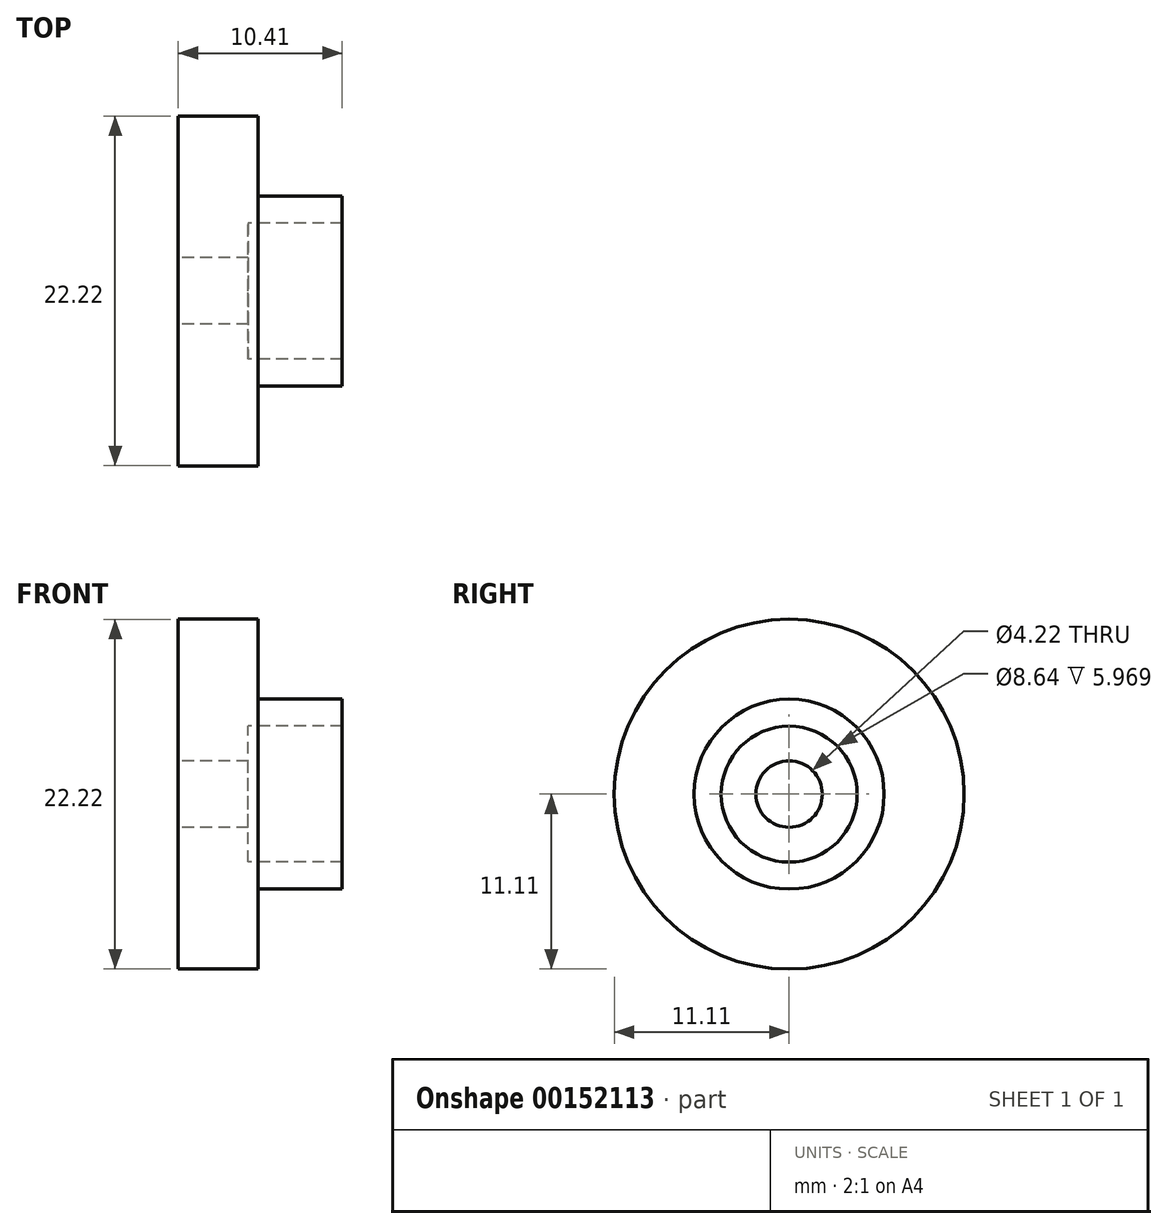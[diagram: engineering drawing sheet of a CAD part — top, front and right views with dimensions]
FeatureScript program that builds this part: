
annotation { "Feature Type Name" : "Feature", "Feature Type Description" : "" }
export const myFeature = defineFeature(function(context is Context, id is Id, definition is map)
    precondition{}
    {
        {
            var Q0;
            Q0=qCreatedBy(makeId("Right.planeOp"),FACE);
            var sketch = newSketch(context, id + "F0", { "sketchPlane" : qUnion([Q0])});
            skCircle(sketch, "E0", {"center": v(0, 0) * mm, "radius": 11.11 * mm});
            skCircle(sketch, "E1", {"center": v(0, 0) * mm, "radius": 6.03 * mm});
            skCircle(sketch, "E2", {"center": v(0, 0) * mm, "radius": 2.1 * mm});
            skCircle(sketch, "E3", {"center": v(0, 0) * mm, "radius": 4.32 * mm});
            skSolve(sketch);
        }
        {
            var Q0;
            Q0=makeQuery(id+"F0.imprint","IMPRINT",FACE,{"disambiguationData":[TD([[makeQuery(id+"F0.imprint","IMPRINT",EDGE,{"derivedFrom":sQuery(id+"F0.wireOp",EDGE,"E0")}),1.0]])]});
            var Q1;
            Q1=makeQuery(id+"F0.imprint","IMPRINT",FACE,{"disambiguationData":[TD([[makeQuery(id+"F0.imprint","IMPRINT",EDGE,{"derivedFrom":sQuery(id+"F0.wireOp",EDGE,"E1")}),1.0]])]});
            var Q2;
            Q2=makeQuery(id+"F0.imprint","IMPRINT",FACE,{"disambiguationData":[TD([[makeQuery(id+"F0.imprint","IMPRINT",EDGE,{"derivedFrom":sQuery(id+"F0.wireOp",EDGE,"E2")}),-1.0]])]});
            extrude(context, id + "F1", {"entities" : qUnion([Q0, Q1, Q2]), "depth" : 5.08 * mm});
        }
        {
            var Q0;
            Q0=makeQuery(id+"F0.imprint","IMPRINT",FACE,{"disambiguationData":[TD([[makeQuery(id+"F0.imprint","IMPRINT",EDGE,{"derivedFrom":sQuery(id+"F0.wireOp",EDGE,"E1")}),1.0]])]});
            var Q1;
            Q1=makeQuery(id+"F0.imprint","IMPRINT",FACE,{"disambiguationData":[TD([[makeQuery(id+"F0.imprint","IMPRINT",EDGE,{"derivedFrom":sQuery(id+"F0.wireOp",EDGE,"E2")}),-1.0]])]});
            extrude(context, id + "F2", {"entities" : qUnion([Q0, Q1]), "operationType" : NewBodyOperationType.ADD, "depth" : 10.4 * mm});
        }
        {
            var Q0;
            Q0=makeQuery(id+"F0.imprint","IMPRINT",FACE,{"disambiguationData":[TD([[makeQuery(id+"F0.imprint","IMPRINT",EDGE,{"derivedFrom":sQuery(id+"F0.wireOp",EDGE,"E2")}),-1.0]])]});
            extrude(context, id + "F3", {"entities" : qUnion([Q0]), "operationType" : NewBodyOperationType.REMOVE, "depth" : 12.7 * mm, "hasSecondDirection" : true, "secondDirectionOppositeDirection" : false, "secondDirectionDepth" : 4.44 * mm});
        }
    });
